# Revit family: Window_Shade-Draper_Inc.-Access_Dual_Roller_Flexshade
name_source: partatom
category: Specialty Equipment
revit_build: Autodesk Revit Architecture 2012 (Build: 20110309_2315(x64)
units: mm (PartAtom-declared; Revit-internal decimal feet)

## types (12) — shared parameters
Depth = 4 3/4"
Description = Dual Roller Shade
Fascia Material = Paint - Draper - White
Front Shade Material = Fabric - Draper - Green Screen Revive 5%
LightBloc Channel = No
Manufacturer = Draper Inc.
Model = Dual Roller FlexShade
Number of Poles = 1
Phase = 1
Product Documentation Link = http://www.draperinc.com
Product Name = Dual Roller
Product Page URL = http://www.draperinc.com
URL = http://www.DraperInc.com
Width = 7"

## per-type parameters (varying)
| type | Apparent Load | Back Shade Material | Bead Chain | Brackets Only | C Heigth | C Length | Dim A | Frequency | Head Box | Length | Overall Height | Power Factor | Voltage |
| Headbox - 110V Standard/ILT | 132 VA | Fabric - Draper - SunBloc - Series SB900 | No | No | 5' - 9 1/2" | 8' - 2 7/8" | 7/8" | 60 Hz | Yes | 8' - 2 7/8" | 5' - 9 1/2" | 1 | 110 V |
| Headbox - 220V Standard/ILT | 132 VA | Fabric - Draper - SunBloc - Series SB900 | No | No | 5' - 9 1/2" | 8' - 2 7/8" | 7/8" | 60 Hz | Yes | 8' - 2 7/8" | 5' - 9 1/2" | 1 | 220 V |
| Headbox - 110V Quiet | 132 VA | Fabric - Draper - SunBloc - Series SB900 | No | No | 5' - 9 1/2" | 8' - 2 7/8" | 31/32" | 60 Hz | Yes | 8' - 2 7/8" | 5' - 9 1/2" | 1 | 110 V |
| Headbox - 220V Quiet | 132 VA | Fabric - Draper - SunBloc - Series SB900 | No | No | 5' - 9 1/2" | 8' - 2 7/8" | 31/32" | 60 Hz | Yes | 8' - 2 7/8" | 5' - 9 1/2" | 1 | 110 V |
| Headbox - Battery/24V | 0 VA | Paint - Draper - White | No | No | 5' - 9 1/2" | 8' - 2 7/8" | 31/32" | 0 Hz | Yes | 8' - 2 7/8" | 5' - 9 1/2" | 0 | 0 V |
| Headbox - Bead Chain Clutch | 0 VA | Fabric - Draper - SunBloc - Series SB900 | Yes | No | 3' - 0" | 3' - 0" | 31/32" | 0 Hz | Yes | 3' - 0" | 3' - 0" | 0 | 0 V |
| Brackets Only - 110V Quiet | 132 VA | Fabric - Draper - SunBloc - Series SB900 | No | Yes | 5' - 9 1/2" | 8' - 2 7/8" | 31/32" | 60 Hz | No | 8' - 2 7/8" | 5' - 9 1/2" | 1 | 110 V |
| Brackets Only - 110V Standard/ILT | 132 VA | Fabric - Draper - SunBloc - Series SB900 | No | Yes | 5' - 9 1/2" | 8' - 2 7/8" | 7/8" | 60 Hz | No | 8' - 2 7/8" | 5' - 9 1/2" | 1 | 110 V |
| Brackets Only - 220V Quiet | 132 VA | Fabric - Draper - SunBloc - Series SB900 | No | Yes | 5' - 9 1/2" | 8' - 2 7/8" | 31/32" | 60 Hz | No | 8' - 2 7/8" | 5' - 9 1/2" | 1 | 110 V |
| Brackets Only - 220V Standard/ILT | 132 VA | Fabric - Draper - SunBloc - Series SB900 | No | Yes | 5' - 9 1/2" | 8' - 2 7/8" | 7/8" | 60 Hz | No | 8' - 2 7/8" | 5' - 9 1/2" | 1 | 220 V |
| Brackets Only - Battery/24V | 0 VA | Paint - Draper - White | No | Yes | 5' - 9 1/2" | 8' - 2 7/8" | 31/32" | 0 Hz | No | 8' - 2 7/8" | 5' - 9 1/2" | 0 | 0 V |
| Brackets Only - Bead Chain Clutch | 0 VA | Fabric - Draper - SunBloc - Series SB900 | Yes | No | 3' - 0" | 3' - 0" | 31/32" | 0 Hz | Yes | 3' - 0" | 3' - 0" | 0 | 0 V |

## geometry (parser evidence)
native form markers: Blend x5, Sweep x13
no freeform markers — native parametric forms only
